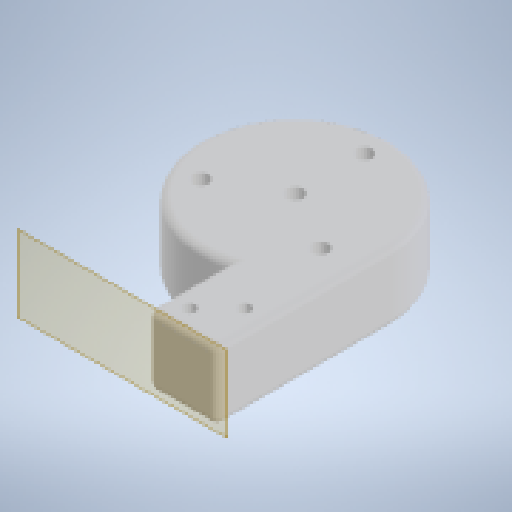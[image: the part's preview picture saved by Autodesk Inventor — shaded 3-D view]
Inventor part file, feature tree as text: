
AUTODESK INVENTOR PART (.ipt)
format: ipt  version: 2024 (Build 280153000, 153)  size: 208,896 bytes
history: native  units: mm
features: extrude x4, hole x2, plane x1, fillet x1
ambient origin geometry x8: Origin, YZ Plane, XZ Plane, XY Plane, X Axis, Y Axis, Z Axis, Center Point
bodies: Solid1 (feature_tree)
feature tree (8):
  extrude  "Extrusion1"  Depth=55.0mm
  plane  "Work Plane1"
  extrude  "Extrusion4"  Depth=20.0mm TaperAngle=0.0deg
  hole  "Hole1"  [1 undecoded]
  fillet  "Fillet2"  Radius=8.0mm
  hole  "Hole2"  [1 undecoded]
  extrude  "Extrusion2"  Depth=40.0mm
  extrude  "Extrusion5"  Depth=30.0mm TaperAngle=360.0deg
note: 2 required parameter values undecoded (feature->parameter linkage not recoverable at this tier; creation-order binding heuristic only, values carry confidence <= 0.55)
